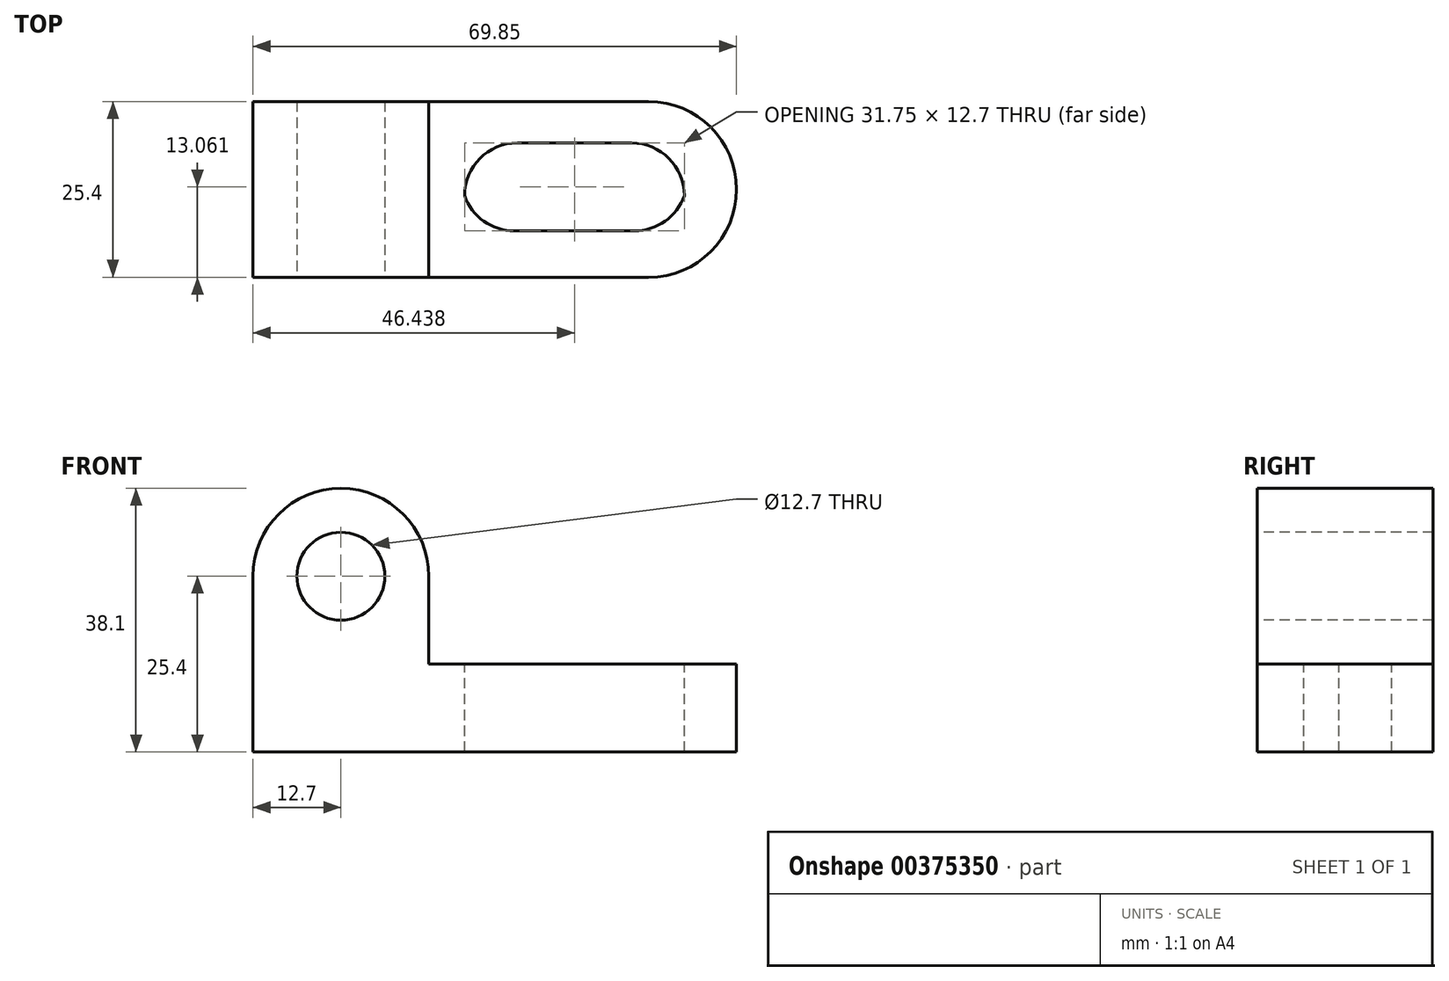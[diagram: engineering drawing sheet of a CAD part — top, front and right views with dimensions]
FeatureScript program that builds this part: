
annotation { "Feature Type Name" : "Feature", "Feature Type Description" : "" }
export const myFeature = defineFeature(function(context is Context, id is Id, definition is map)
    precondition{}
    {
        {
            var Q0;
            Q0=qCreatedBy(makeId("Front.planeOp"),FACE);
            var sketch = newSketch(context, id + "F0", { "sketchPlane" : qUnion([Q0])});
            skLineSegment(sketch, "E0", {"start": v(0, 0) * mm, "end": v(0, 38.1) * mm});
            skLineSegment(sketch, "E1", {"start": v(0, 38.1) * mm, "end": v(25.4, 38.1) * mm});
            skLineSegment(sketch, "E2", {"start": v(25.4, 38.1) * mm, "end": v(25.4, 12.7) * mm});
            skLineSegment(sketch, "E3", {"start": v(25.4, 12.7) * mm, "end": v(69.85, 12.7) * mm});
            skLineSegment(sketch, "E4", {"start": v(69.85, 12.7) * mm, "end": v(69.85, 0) * mm});
            skLineSegment(sketch, "E5", {"start": v(69.85, 0) * mm, "end": v(0, 0) * mm});
            skSolve(sketch);
        }
        {
            var Q0;
            Q0 = qSketchRegion(id + "F0", true);
            extrude(context, id + "F1", {"entities" : qUnion([Q0]), "depth" : 25.4 * mm});
        }
        {
            var Q0;
            Q0=makeQuery(id+"F1.opExtrude","CAP_EDGE",EDGE,{"disambiguationData":[OSD([sQuery(id+"F0.wireOp",EDGE,"E4")])],"isStart":false});
            fillet(context, id + "F2", {"entities" : qUnion([Q0]), "radius" : 12.7 * mm, "tangentPropagation" : true, "allowEdgeOverflow" : false});
        }
        {
            var Q0;
            Q0=makeQuery(id+"F1.opExtrude","CAP_EDGE",EDGE,{"disambiguationData":[OSD([sQuery(id+"F0.wireOp",EDGE,"E4")])],"isStart":true});
            fillet(context, id + "F3", {"entities" : qUnion([Q0]), "radius" : 12.7 * mm, "tangentPropagation" : true, "allowEdgeOverflow" : false});
        }
        {
            var Q0;
            Q0=makeQuery(id+"F1.opExtrude","SWEPT_EDGE",EDGE,{"disambiguationData":[OSD([sQuery(id+"F0.wireOp",EDGE,"E1"),sQuery(id+"F0.wireOp",EDGE,"E2")])]});
            fillet(context, id + "F4", {"entities" : qUnion([Q0]), "radius" : 12.7 * mm, "tangentPropagation" : true, "allowEdgeOverflow" : false});
        }
        {
            var Q0;
            Q0=makeQuery(id+"F1.opExtrude","SWEPT_EDGE",EDGE,{"disambiguationData":[OSD([sQuery(id+"F0.wireOp",EDGE,"E0"),sQuery(id+"F0.wireOp",EDGE,"E1")])]});
            fillet(context, id + "F5", {"entities" : qUnion([Q0]), "radius" : 12.7 * mm, "tangentPropagation" : true, "allowEdgeOverflow" : false});
        }
        {
            var Q0;
            Q0=makeQuery(id+"F1.opExtrude","CAP_FACE",FACE,{"disambiguationData":[OSD([sQuery(id+"F0.wireOp",EDGE,"E0"),sQuery(id+"F0.wireOp",EDGE,"E1"),sQuery(id+"F0.wireOp",EDGE,"E2"),sQuery(id+"F0.wireOp",EDGE,"E3"),sQuery(id+"F0.wireOp",EDGE,"E4"),sQuery(id+"F0.wireOp",EDGE,"E5")])],"isStart":false});
            var sketch = newSketch(context, id + "F6", { "sketchPlane" : qUnion([Q0])});
            skCircle(sketch, "E6", {"center": v(12.7, 25.4) * mm, "radius": 6.35 * mm});
            skSolve(sketch);
        }
        {
            var Q0;
            Q0 = qSketchRegion(id + "F6", true);
            extrude(context, id + "F7", {"entities" : qUnion([Q0]), "operationType" : NewBodyOperationType.REMOVE, "oppositeDirection" : true, "depth" : 25.4 * mm});
        }
        {
            var Q0;
            Q0=makeQuery(id+"F1.opExtrude","SWEPT_FACE",FACE,{"disambiguationData":[OSD([sQuery(id+"F0.wireOp",EDGE,"E3")])]});
            var sketch = newSketch(context, id + "F8", { "sketchPlane" : qUnion([Q0])});
            skLineSegment(sketch, "E7", {"start": v(30.56, -5.99) * mm, "end": v(30.56, -18.69) * mm});
            skLineSegment(sketch, "E8", {"start": v(30.56, -18.69) * mm, "end": v(62.31, -18.69) * mm});
            skLineSegment(sketch, "E9", {"start": v(62.31, -18.69) * mm, "end": v(62.31, -5.99) * mm});
            skLineSegment(sketch, "E10", {"start": v(62.31, -5.99) * mm, "end": v(30.56, -5.99) * mm});
            skSolve(sketch);
        }
        {
            var Q0;
            Q0 = qSketchRegion(id + "F8", true);
            extrude(context, id + "F9", {"entities" : qUnion([Q0]), "operationType" : NewBodyOperationType.REMOVE, "oppositeDirection" : true, "depth" : 25.4 * mm});
        }
        {
            var Q0;
            Q0=makeQuery(id+"F9.boolean.opBoolean","COPY",EDGE,{"derivedFrom":makeQuery(id+"F9.opExtrude","SWEPT_EDGE",EDGE,{"disambiguationData":[OSD([sQuery(id+"F8.wireOp",EDGE,"E7"),sQuery(id+"F8.wireOp",EDGE,"E10")])]})});
            fillet(context, id + "F10", {"entities" : qUnion([Q0]), "radius" : 7.62 * mm, "tangentPropagation" : true, "allowEdgeOverflow" : false});
        }
        {
            var Q0;
            Q0=makeQuery(id+"F9.boolean.opBoolean","COPY",EDGE,{"derivedFrom":makeQuery(id+"F9.opExtrude","SWEPT_EDGE",EDGE,{"disambiguationData":[OSD([sQuery(id+"F8.wireOp",EDGE,"E7"),sQuery(id+"F8.wireOp",EDGE,"E8")])]})});
            fillet(context, id + "F11", {"entities" : qUnion([Q0]), "radius" : 7.62 * mm, "tangentPropagation" : true, "allowEdgeOverflow" : false});
        }
        {
            var Q0;
            Q0=makeQuery(id+"F9.boolean.opBoolean","COPY",EDGE,{"derivedFrom":makeQuery(id+"F9.opExtrude","SWEPT_EDGE",EDGE,{"disambiguationData":[OSD([sQuery(id+"F8.wireOp",EDGE,"E9"),sQuery(id+"F8.wireOp",EDGE,"E10")])]})});
            fillet(context, id + "F12", {"entities" : qUnion([Q0]), "radius" : 7.62 * mm, "tangentPropagation" : true, "allowEdgeOverflow" : false});
        }
        {
            var Q0;
            Q0=makeQuery(id+"F9.boolean.opBoolean","COPY",EDGE,{"derivedFrom":makeQuery(id+"F9.opExtrude","SWEPT_EDGE",EDGE,{"disambiguationData":[OSD([sQuery(id+"F8.wireOp",EDGE,"E8"),sQuery(id+"F8.wireOp",EDGE,"E9")])]})});
            fillet(context, id + "F13", {"entities" : qUnion([Q0]), "radius" : 7.62 * mm, "tangentPropagation" : true, "allowEdgeOverflow" : false});
        }
    });
